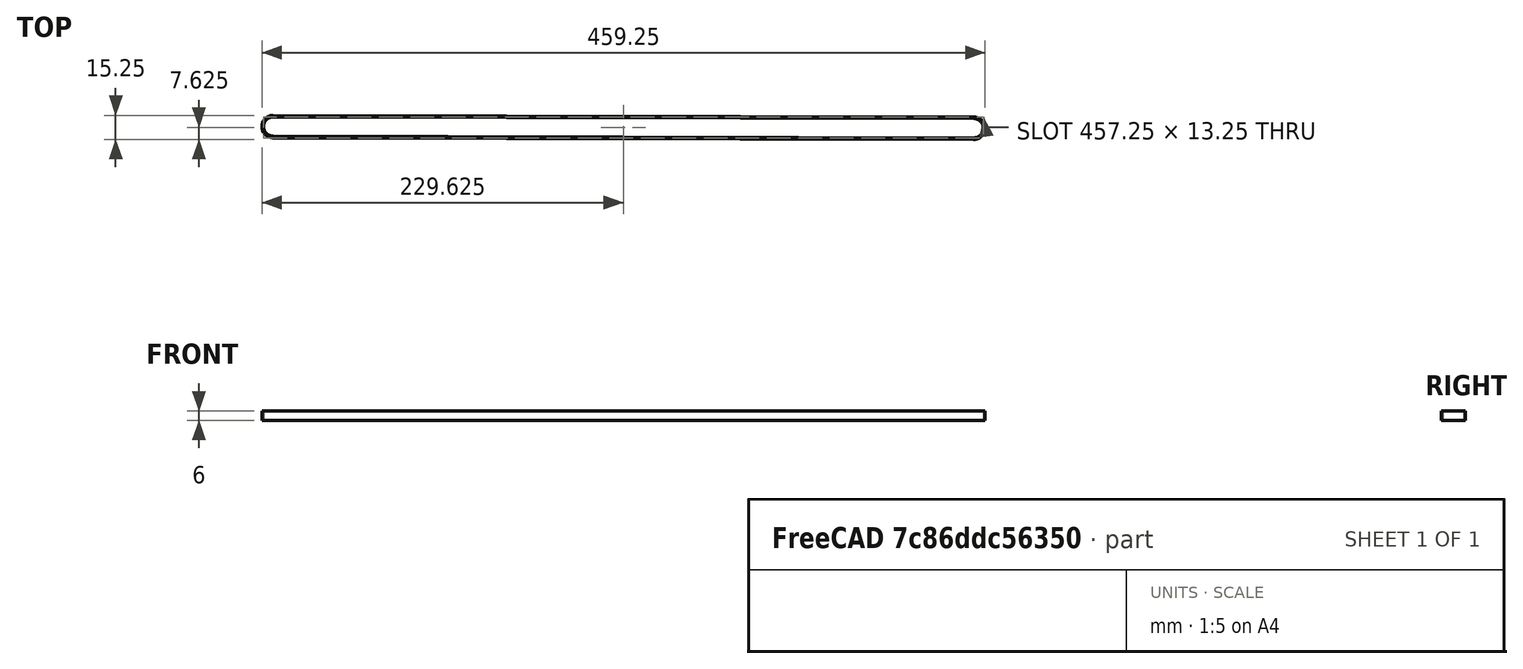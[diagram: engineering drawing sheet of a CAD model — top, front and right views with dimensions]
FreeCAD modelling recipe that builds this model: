
FCSTD DOCUMENT  (FreeCAD 0.19R21858 (Git))
Label: x_axis_2gt_belt
License: All rights reserved
LicenseURL: http://en.wikipedia.org/wiki/All_rights_reserved
objects: Sketcher::SketchObject×1, PartDesign::Pad×1, PartDesign::Body×1, PartDesign::CoordinateSystem×1, App::Part×1
note: 5 computed .brp shape members not serialized (recipe doc carries the construction recipe); baked Part::Feature solids carry a one-line shape summary decoded from their .brp

FEATURE [Sketcher::SketchObject] Sketch045
  MapMode = 5
  Support = -> [XY_Plane049]
  sketch-geometry (8):
    g0: ArcOfCircle CenterX=0 CenterY=0 CenterZ=0 NormalX=0 NormalY=0 NormalZ=1 AngleXU=0 Radius=6.1 StartAngle=1.56866 EndAngle=4.71003
    g1: ArcOfCircle CenterX=445 CenterY=-1 CenterZ=0 NormalX=0 NormalY=0 NormalZ=1 AngleXU=0 Radius=6.15 StartAngle=4.71003 EndAngle=7.85185
    g2: ArcOfCircle CenterX=445 CenterY=-1 CenterZ=0 NormalX=0 NormalY=0 NormalZ=1 AngleXU=0 Radius=7.15 StartAngle=4.71003 EndAngle=7.85185
    g3: ArcOfCircle CenterX=0 CenterY=0 CenterZ=0 NormalX=0 NormalY=0 NormalZ=1 AngleXU=0 Radius=7.1 StartAngle=1.56866 EndAngle=4.71003
    g4: LineSegment StartX=0.0151573 StartY=7.09998 StartZ=0 EndX=445.015 EndY=6.14998 EndZ=0
    g5: LineSegment StartX=445.013 StartY=5.14999 StartZ=0 EndX=0.0130224 EndY=6.09999 EndZ=0
    g6: LineSegment StartX=-0.0143932 StartY=-6.09998 StartZ=0 EndX=444.985 EndY=-7.14998 EndZ=0
    g7: LineSegment StartX=444.983 StartY=-8.14998 StartZ=0 EndX=-0.0167528 EndY=-7.09998 EndZ=0
  constraints (17):
    c: Diameter(g1) = 12.3
    c: Coincident(g2,g1)
    c: Diameter(g2) = 14.3
    c: Diameter(g0) = 12.2
    c: Coincident(g3,g0)
    c: Diameter(g3) = 14.2
    c: DistanceX(g-1,g1) = 445
    c: Tangent(g2,g7) = 1.5708
    c: Tangent(g1,g5) = -1.5708
    c: Tangent(g3,g7) = 1.5708
    c: Tangent(g3,g4) = 1.5708
    c: Tangent(g0,g6) = -1.5708
    c: Tangent(g0,g5) = -1.5708
    c: Tangent(g4,g2) = 1.5708
    c: Tangent(g1,g6) = -1.5708
    c: DistanceY(g1,g0) = 1
    c: Coincident(g0,g-1)
FEATURE [PartDesign::Pad] Pad019
  AllowMultiFace = false
  Length = 6
  Length2 = 100
  Midplane = true
  Profile = -> Sketch045
  Type = 0
FEATURE [PartDesign::Body] Body018  label="Body"
  Group = -> [Sketch045,Pad019]
  Origin = -> Origin049
  Tip = -> Pad019
FEATURE [PartDesign::CoordinateSystem] LCS_1
  AttacherType = Attacher::AttachEngine3D
  AttachmentOffset = pos=(0,0,-3) rot=(0,0,1;0rad)
  MapMode = 11
  Placement = pos=(0,0,4e-16) rot=(0,0,1;3.13946rad)
  Support = -> [Pad019]
FEATURE [App::Part] Part029  label="x_axis_2gt_belt"
  Group = -> [Body018,LCS_1]
  Origin = -> Origin043
